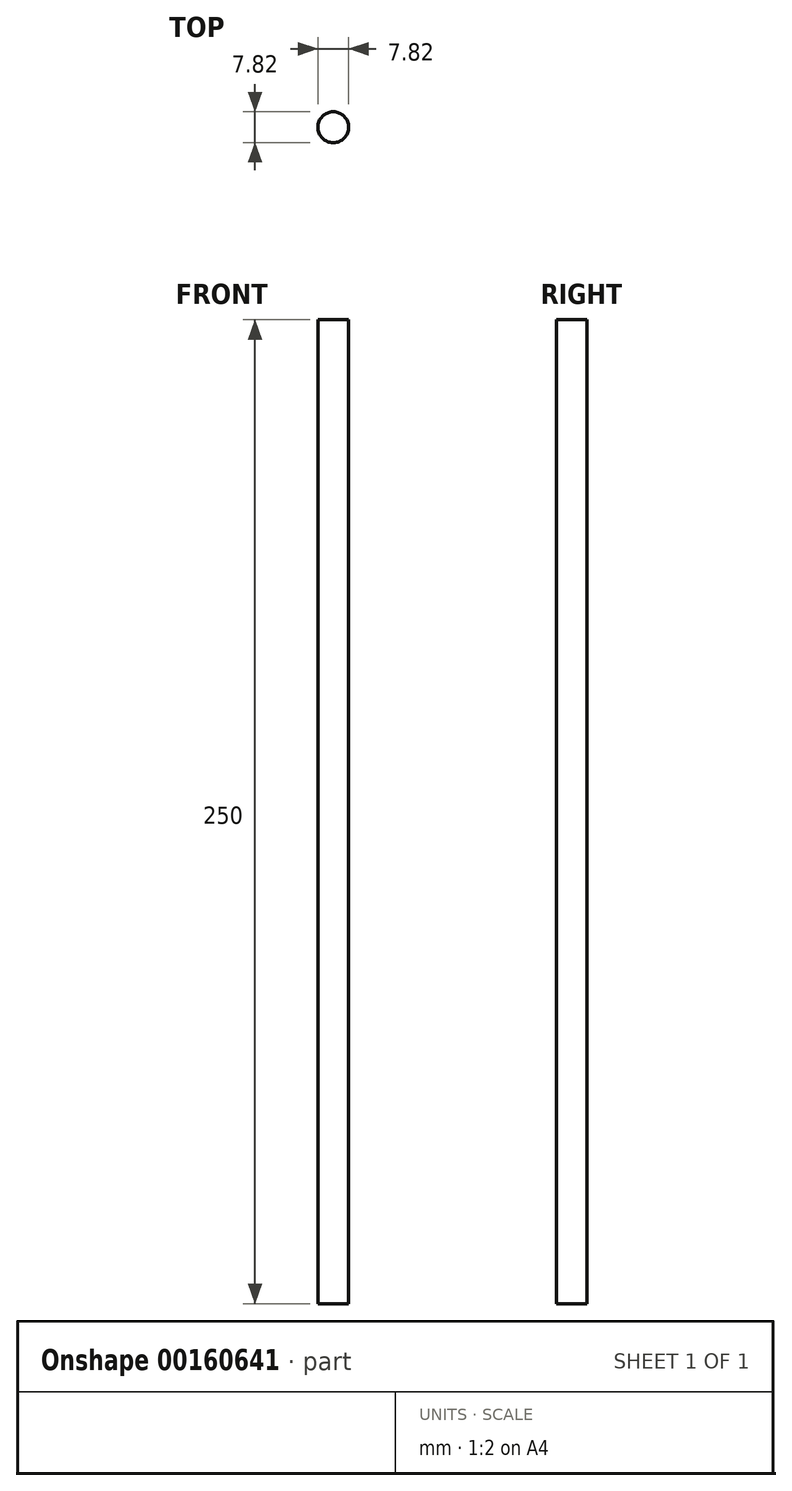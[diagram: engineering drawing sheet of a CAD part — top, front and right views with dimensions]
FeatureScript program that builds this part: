
annotation { "Feature Type Name" : "Feature", "Feature Type Description" : "" }
export const myFeature = defineFeature(function(context is Context, id is Id, definition is map)
    precondition{}
    {
        {
            var Q0;
            Q0=qCreatedBy(makeId("Top.planeOp"),FACE);
            var sketch = newSketch(context, id + "F0", { "sketchPlane" : qUnion([Q0])});
            skCircle(sketch, "E0", {"center": v(0, 0) * mm, "radius": 3.91 * mm});
            skCircle(sketch, "E1", {"center": v(10, 0) * mm, "radius": 3.91 * mm});
            skCircle(sketch, "E2", {"center": v(20, 0) * mm, "radius": 3.88 * mm});
            skCircle(sketch, "E3", {"center": v(30, 0) * mm, "radius": 3.88 * mm});
            skSolve(sketch);
        }
        {
            var Q0;
            Q0=makeQuery(id+"F0.imprint","IMPRINT",FACE,{"disambiguationData":[TD([[makeQuery(id+"F0.imprint","IMPRINT",EDGE,{"derivedFrom":sQuery(id+"F0.wireOp",EDGE,"E0")}),1.0]])]});
            extrude(context, id + "F1", {"entities" : qUnion([Q0]), "depth" : 250 * mm});
        }
    });
